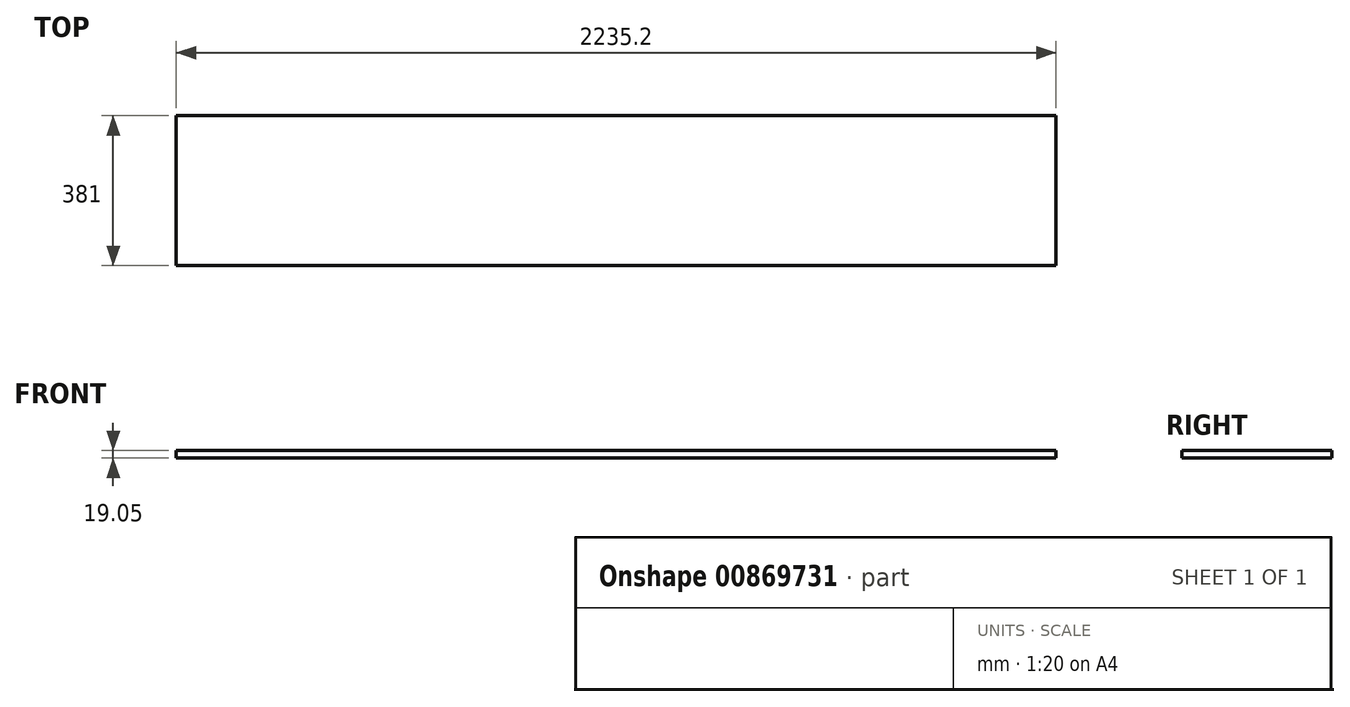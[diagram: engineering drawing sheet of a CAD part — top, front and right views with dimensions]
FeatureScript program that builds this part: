
annotation { "Feature Type Name" : "Feature", "Feature Type Description" : "" }
export const myFeature = defineFeature(function(context is Context, id is Id, definition is map)
    precondition{}
    {
        {
            var Q0;
            Q0=qCreatedBy(makeId("Top.planeOp"),FACE);
            var sketch = newSketch(context, id + "F0", { "sketchPlane" : qUnion([Q0])});
            skLineSegment(sketch, "E0.bottom", {"start": v(0, 0) * mm, "end": v(2235.2, 0) * mm});
            skLineSegment(sketch, "E0.top", {"start": v(0, -381) * mm, "end": v(2235.2, -381) * mm});
            skLineSegment(sketch, "E0.left", {"start": v(0, 0) * mm, "end": v(0, -381) * mm});
            skLineSegment(sketch, "E0.right", {"start": v(2235.2, 0) * mm, "end": v(2235.2, -381) * mm});
            skSolve(sketch);
        }
        {
            var Q0;
            Q0 = qSketchRegion(id + "F0", true);
            extrude(context, id + "F1", {"entities" : qUnion([Q0]), "depth" : 19.05 * mm, "offsetDistance" : 25.4 * mm});
        }
    });
